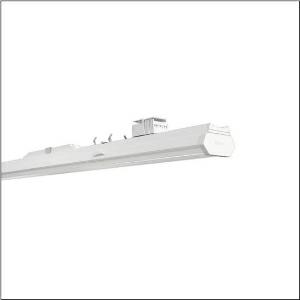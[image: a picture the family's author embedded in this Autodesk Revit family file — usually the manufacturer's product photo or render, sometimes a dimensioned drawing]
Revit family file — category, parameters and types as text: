
# Revit family: licross_r__11_protected_ho_51tp12cn3d5m_d34a
name_source: partatom
category: Lighting Fixtures
units: mm (PartAtom-declared; Revit-internal decimal feet)

## family parameters
Cut with Voids When Loaded = No
Host = Face
Light Source = No
Part Type = Normal
Room Calculation Point = No
Round Connector Dimension = Use Diameter
Shared = No

## types (1)
- --- (1 x LED, 13690 lm, 77.6 W, 3000K)
    Apparent Load = 78 VA
    CIE Flux Codes = 70 91 97 98 100
    Color Rendering = 80
    Color Temperature = 3000K
    Default Elevation = 1800 mm
    Description = Licross® 11 Protected HO, luminaire insert, of sheet steel, galvanised, coil coated, white, length: 1.500mm, width: 90mm, height: 101mm, LED rated luminous flux: 13.690lm, light colour: 830, control gear: ON/OFF Multilumen, CLOi, with plug, 3-pole, with phase selection, mains connection: 220..240V, AC, 50/60Hz, start of lifetime: 78W, end of service life: 87W, halogen-free wiring, primary light control with lens, of plastic, primary optical cover: cover, of PMMA, light emission: direct distribution, primary light characteristic: symmetric, protection rating (complete): IP64, insulation class (complete): insulation class I (protective earthing), certification: CE, ENEC, VDE, UKCA, protection symbol: D if used in an environment with conductive dust loads with corresponding accessories, impact resistance: IK06, permissible ambient temperature for indoor applications: -35..+35°C, corresponds to IFS (International Featured Standards) requirements for safety and quality in the food industry, reducing of maximum allowable ambient temperature of 5°C with ceiling mounting, LABS conformity tested according to VDMA 24364:2018-05, packaging unit: 1 piece
    Height = 92 mm
    Lamp = 1 x LED
    Lamp Light Flux = 13690 lm
    Lamp Power = 77.6 W
    Lamp count = 1
    Length = 1500 mm
    Luminous efficacy = 176 lm/W
    Manufacturer = Siteco
    ModVariant = No
    Model = 51TP12CN3D5M
    Mounting Place = Ceiling
    Mounting Type = Pendant
    Number of Poles = 1
    OnlyDefault = Yes
    Power Factor = 1
    Product Name = Licross® 11 Protected HO
    Product group = luminaire insert
    ProductGroupID = 902
    Protection Class = Protection class I
    Protection Degree = IP 64
    RLX_Detail_Level = 1
    RLX_Emergency_Light_Flux = 0 lm
    RLX_Emergency_Type = 0
    RLX_Emergency_Type_DB = No
    RlxData = <blob elided: 22193 chars, md5=6d5f6810>
    Socket = socket
    Standby Power = 0 W
    System Light Flux = 13690 lm
    System Power = 78 W
    Type Comments = factory setting: luminous flux: 100 % | (A | C | E) | 181 mA
    Type Image = l_1256148.jpg
    URL = http://relux.com
    VarID = @adj_010851
    Voltage = 0 V
    Weight = 0.00 kg
    Width = 88 mm

## geometry (parser evidence)
native form markers: Blend x4, Sweep x13
no freeform markers — native parametric forms only
